SOLIDWORKS PART (.sldprt)
format: sldprt  version: not decoded by parser v0  size: 190,464 bytes
history: native  units: mm
features: sketch x4, cut_extrude x3, chamfer x2, material x1, extrude x1 (+13 scaffold rows collapsed)
feature tree (24):
  scaffold x13  (default folders/planes/origin — collapsed)
  material  "Material <not specified>"
  sketch  "Sketch1"  dims[c1.D1=5.0mm c1.D2=65.25mm c1.D3=3.0mm c2.D2=3.0mm]
  extrude  "Boss-Extrude1"  Depth=15mm
  sketch  "Sketch2"  dims[D1=10.0mm D2=10.0mm D3=~2.862439mm]
  cut_extrude  "Cut-Extrude1"  [1 undecoded]
  chamfer  "Chamfer1"  Distance=10mm Angle=45deg
  sketch  "Sketch5"  dims[D1=0.0mm]
  cut_extrude  "Cut-Extrude2"  [1 undecoded]
  sketch  "Sketch6"  dims[D1=0.0mm]
  cut_extrude  "Cut-Extrude3"  [1 undecoded]
  chamfer  "Chamfer2"  Distance=1mm Angle=45deg
decode coverage: 7 of 10 modeling features carry decoded parameters
note: ~ marks probable driven/reference dimensions
note: 3 parameter values undecoded
summary: no parameter record found for 3 features
note: suppression state not decoded; provenance and decode notes live in map.json
